# Revit family: KDW010050
name_source: partatom
category: Plumbing Fixtures
revit_build: Autodesk Revit 2015 (Build: 20140606_1530(x64)
units: mm (PartAtom-declared; Revit-internal decimal feet)

## types (1)
- KDW010050
    BIMobject category = Bath & Spas
    Brand url = http://www.kaldewei.com
    Color = https://www.kaldewei.co.uk
    ColourOptions = https://www.kaldewei.co.uk
    ConnectingDimensions = EN 232
    Design country = Germany
    DrainSize = 90 mm
    Durability = https://www.kaldewei.de
    Edition number = 1
    Features = https://www.kaldewei.co.uk
    Finish = https://www.kaldewei.co.uk
    Finition = Kaldewei
    HasGrabHandles = https://www.kaldewei.co.uk
    IFC Classification = Furnishing Element
    IfcExportAs = BATH
    IfcExportType = IfcSanitaryTerminalType
    IntegralAccessories = https://www.kaldewei.co.uk
    Manufacturer = Kaldewei
    Manufacturer country = Germany
    ManufacturerCountry = GERMANY
    ManufacturerName = KALDEWEI
    ManufacturerURL = https://www.kaldewei.com
    Material = steel enamel
    Material main = Steel
    Material secondary = Enamel
    Model = CONODUO
    NBS Reference Code = 35-06-08
    NBS Reference Description = Baths
    Name = CONODUO
    Nominal height = 750 cm
    Nominal width = 1700 cm
    NominalDepth = 445
    NominalLength = 1700
    ObjectName = CONODUO 750x1700x445
    ObjectNorm = EN 14516EU DECLARATION OF PERFORMANCE(https://www.kaldewei.de
    ObjectPicture = https://www.kaldewei.co.uk
    ObjectURL = https://www.kaldewei.co.uk
    Polantis code = KDW010050
    Product Guid = c17481f0-5bce-41dc-bf18-a227a1ab67a6
    Product SKU = 732
    Product certification = https://www.kaldewei.co.uk
    Product data url = https://bimobject.com
    Product family = CONODUO
    Product group = Bathtub
    Product url = https://www.kaldewei.co.uk
    ProductInformation = Model No.732: CONODUO unites independent design and excellent bathing comfort for a sense of peace and clarity. Architectonic and geometric elements merge to create a distinctive form. Other special features include the concealed outflow with enamelled cover and an enamelled knob for outflow control.
    QR code = http://bimobject.com
    Revision = 1
    SerialNumber = 732
    Shape = Rectangular baths
    Size = 750x1700x445
    SupportFrame = https://www.kaldewei.co.uk
    Sustainability = https://kaldewei-fa.secure.footprint.net
    Technical description = https://www.kaldewei.co.uk
    TechnicalDataURL = https://kaldewei.typo-live.web-factory.de
    Type Comments = CONODUO 732 750x1700x445
    UNSPSC Code = 30181501
    UNSPSCCode = 30181500
    UNSPSCNames = Sanitary ware
    URL = https://www.kaldewei.co.uk
    Uniclass 1.4 Code = L7211
    Uniclass 1.4 Description = Baths
    Uniclass 2.0 Code = PR-35-06-08
    Uniclass 2.0 Description = Baths
    Uniclass 2015 = Pr_40_20_06_08
    Version = 5
    VolumeToOverflowMaximum = 122
    WarrantyDurationParts = 30
    WarrantyDurationUnit = Year
    WarrantyStartDate = https://www.kaldewei.co.uk
    WaterSupplyOverflowAndWasteHolesOverflow = 52 mm
    WaterSupplyOverflowAndWasteHolesWaste = 90 mm
    Weight = 52
    Weight Net (Kg) = 52

## geometry (parser evidence)
native form markers: Sweep x3
no freeform markers — native parametric forms only
